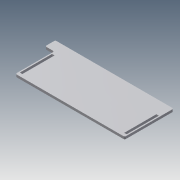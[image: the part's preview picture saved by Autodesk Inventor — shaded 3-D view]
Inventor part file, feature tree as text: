
AUTODESK INVENTOR PART (.ipt)
format: ipt  version: 2014 (Build 180170000, 170)  size: 114,688 bytes
history: native  units: mm
features: extrude x3, sketch x3, fillet x2
ambient origin geometry x8: Origin, YZ Plane, XZ Plane, XY Plane, X Axis, Y Axis, Z Axis, Center Point
bodies: Solid1 (feature_tree)
feature tree (8):
  extrude  "Extrusion1"  Depth=268.0mm
  extrude  "Extrusion2"  Depth=6.25mm
  fillet  "Fillet2"  Radius=2.875mm
  extrude  "Extrusion3"  Depth=3.0mm
  fillet  "Fillet3"  Radius=25.0mm
  sketch  "Sketch1"  dims[d0=95.0mm d1=268.0mm]
  sketch  "Sketch2"  dims[d2=6.0mm d3=0.0mm d4=6.25mm d5=2.875mm]
  sketch  "Sketch3"  dims[d8=10.0mm d9=0.0mm d11=3.0mm d12=25.0mm d13=25.0mm d15=6.0mm d16=0.0mm d17=3.0mm d23=8.0mm d24=2.875mm]
